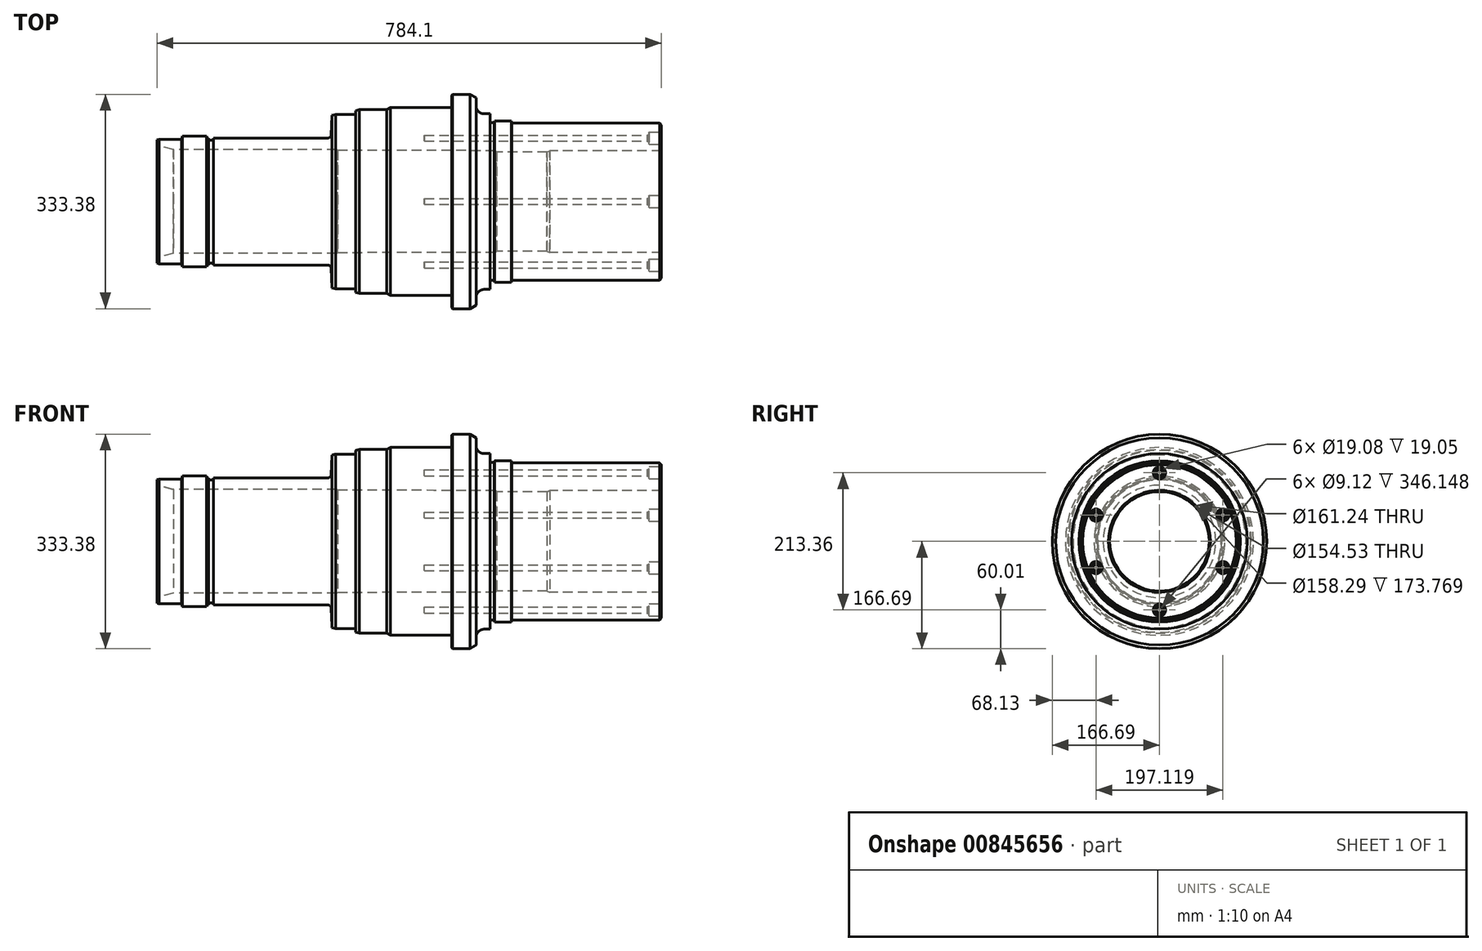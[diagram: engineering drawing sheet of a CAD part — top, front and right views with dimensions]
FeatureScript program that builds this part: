
annotation { "Feature Type Name" : "Feature", "Feature Type Description" : "" }
export const myFeature = defineFeature(function(context is Context, id is Id, definition is map)
    precondition{}
    {
        {
            var Q0;
            Q0=qCreatedBy(makeId("Front.planeOp"),FACE);
            var sketch = newSketch(context, id + "F0", { "sketchPlane" : qUnion([Q0])});
            skLineSegment(sketch, "E0", {"start": v(0, 0) * mm, "end": v(784.1, 0) * mm, "construction": true});
            skLineSegment(sketch, "E1", {"start": v(0, 96.84) * mm, "end": v(38.1, 96.84) * mm});
            skLineSegment(sketch, "E2", {"start": v(25.55, 80.62) * mm, "end": v(279.4, 80.62) * mm});
            skLineSegment(sketch, "E3", {"start": v(39.38, 101.6) * mm, "end": v(77, 101.6) * mm});
            skLineSegment(sketch, "E4", {"start": v(77.72, 98.87) * mm, "end": v(80.16, 98.87) * mm});
            skLineSegment(sketch, "E5", {"start": v(80.16, 98.87) * mm, "end": v(80.16, 95.7) * mm});
            skLineSegment(sketch, "E6", {"start": v(80.16, 95.7) * mm, "end": v(88.09, 95.7) * mm});
            skLineSegment(sketch, "E7", {"start": v(88.09, 95.7) * mm, "end": v(88.09, 98.87) * mm});
            skLineSegment(sketch, "E8", {"start": v(88.09, 98.87) * mm, "end": v(270.59, 98.87) * mm});
            skLineSegment(sketch, "E9", {"start": v(272.2, 135.64) * mm, "end": v(308.69, 135.64) * mm});
            skLineSegment(sketch, "E10", {"start": v(308.69, 135.64) * mm, "end": v(308.69, 142.88) * mm});
            skLineSegment(sketch, "E11", {"start": v(308.69, 142.88) * mm, "end": v(357.2, 142.88) * mm});
            skLineSegment(sketch, "E12", {"start": v(357.2, 142.87) * mm, "end": v(362.7, 146.05) * mm});
            skLineSegment(sketch, "E13", {"start": v(362.7, 146.05) * mm, "end": v(457.99, 146.05) * mm});
            skLineSegment(sketch, "E14", {"start": v(457.99, 146.05) * mm, "end": v(457.99, 166.69) * mm});
            skLineSegment(sketch, "E15", {"start": v(457.99, 166.69) * mm, "end": v(495.94, 166.69) * mm});
            skLineSegment(sketch, "E16", {"start": v(495.94, 166.69) * mm, "end": v(495.94, 136.53) * mm});
            skLineSegment(sketch, "E17", {"start": v(495.94, 136.53) * mm, "end": v(517.52, 136.53) * mm});
            skLineSegment(sketch, "E18", {"start": v(517.52, 136.53) * mm, "end": v(517.52, 122.5) * mm});
            skLineSegment(sketch, "E19", {"start": v(517.52, 122.5) * mm, "end": v(523.88, 122.5) * mm});
            skLineSegment(sketch, "E20", {"start": v(523.88, 122.5) * mm, "end": v(524.65, 125.41) * mm});
            skLineSegment(sketch, "E21", {"start": v(524.65, 125.41) * mm, "end": v(550.85, 125.41) * mm});
            skLineSegment(sketch, "E22", {"start": v(550.85, 125.41) * mm, "end": v(551.7, 122.24) * mm});
            skLineSegment(sketch, "E23", {"start": v(551.7, 122.24) * mm, "end": v(784.1, 122.24) * mm});
            skLineSegment(sketch, "E24", {"start": v(784.1, 79.15) * mm, "end": v(784.1, 122.24) * mm});
            skLineSegment(sketch, "E25", {"start": v(784.1, 79.15) * mm, "end": v(610.33, 79.15) * mm});
            skLineSegment(sketch, "E26", {"start": v(610.33, 79.15) * mm, "end": v(606.3, 77.27) * mm});
            skLineSegment(sketch, "E27", {"start": v(606.3, 77.27) * mm, "end": v(527.92, 77.27) * mm});
            skLineSegment(sketch, "E28", {"start": v(279.4, 80.62) * mm, "end": v(281.23, 79.57) * mm});
            skLineSegment(sketch, "E29", {"start": v(281.23, 79.57) * mm, "end": v(526.04, 79.15) * mm});
            skLineSegment(sketch, "E30", {"start": v(527.92, 77.27) * mm, "end": v(526.04, 79.15) * mm});
            skLineSegment(sketch, "E31", {"start": v(270.59, 98.87) * mm, "end": v(272.2, 135.64) * mm});
            skLineSegment(sketch, "E32", {"start": v(38.1, 96.84) * mm, "end": v(39.38, 101.6) * mm});
            skLineSegment(sketch, "E33", {"start": v(77.72, 98.87) * mm, "end": v(77, 101.6) * mm});
            skPoint(sketch, "E34.end.orphan", {"position": v(38.1, 101.6) * mm});
            skLineSegment(sketch, "E35", {"start": v(0, 87.46) * mm, "end": v(25.55, 80.62) * mm});
            skLineSegment(sketch, "E36", {"start": v(0, 96.84) * mm, "end": v(0, 87.46) * mm});
            skSolve(sketch);
        }
        {
            var Q0;
            Q0 = qSketchRegion(id + "F0", true);
            var Q1;
            Q1=sQuery(id+"F0.wireOp",EDGE,"E0");
            revolve(context, id + "F1", {"surfaceOperationType" : NewSurfaceOperationType.NEW, "entities" : qUnion([Q0]), "axis" : qUnion([Q1]), "revolveType" : RevolveType.FULL});
        }
        {
            var Q0;
            Q0=makeQuery(id+"F1.opRevolve","SWEPT_EDGE",EDGE,{"disambiguationData":[OSD([sQuery(id+"F0.wireOp",EDGE,"E15"),sQuery(id+"F0.wireOp",EDGE,"E16")])]});
            chamfer(context, id + "F2", {"entities" : qUnion([Q0]), "chamferType" : ChamferType.OFFSET_ANGLE, "width" : 9.52 * mm, "oppositeDirection" : false, "angle" : 30 * degree, "tangentPropagation" : true});
        }
        {
            var Q0;
            Q0=makeQuery(id+"F1.opRevolve","SWEPT_EDGE",EDGE,{"disambiguationData":[OSD([sQuery(id+"F0.wireOp",EDGE,"E16"),sQuery(id+"F0.wireOp",EDGE,"E17")])]});
            fillet(context, id + "F3", {"entities" : qUnion([Q0]), "radius" : 12.7 * mm, "tangentPropagation" : true, "allowEdgeOverflow" : false});
        }
        {
            var Q0;
            Q0=makeQuery(id+"F1.opRevolve","SWEPT_EDGE",EDGE,{"disambiguationData":[OSD([sQuery(id+"F0.wireOp",EDGE,"E8"),sQuery(id+"F0.wireOp",EDGE,"E31")])]});
            fillet(context, id + "F4", {"entities" : qUnion([Q0]), "radius" : 5.08 * mm, "tangentPropagation" : true, "allowEdgeOverflow" : false});
        }
        {
            var Q0;
            Q0=makeQuery(id+"F1.opRevolve","SWEPT_EDGE",EDGE,{"disambiguationData":[OSD([sQuery(id+"F0.wireOp",EDGE,"E9"),sQuery(id+"F0.wireOp",EDGE,"E31")])]});
            var Q1;
            Q1=makeQuery(id+"F1.opRevolve","SWEPT_EDGE",EDGE,{"disambiguationData":[OSD([sQuery(id+"F0.wireOp",EDGE,"E10"),sQuery(id+"F0.wireOp",EDGE,"E11")])]});
            chamfer(context, id + "F5", {"entities" : qUnion([Q0, Q1]), "chamferType" : ChamferType.OFFSET_ANGLE, "width" : 1.27 * mm, "oppositeDirection" : false, "angle" : 75 * degree, "tangentPropagation" : true});
        }
        {
            var Q0;
            Q0=makeQuery(id+"F1.opRevolve","SWEPT_EDGE",EDGE,{"disambiguationData":[OSD([sQuery(id+"F0.wireOp",EDGE,"E1"),sQuery(id+"F0.wireOp",EDGE,"SCYpA8kQ-7sTV-xUNJ-m1pp-K6qHX3d4gstn")])]});
            chamfer(context, id + "F6", {"entities" : qUnion([Q0]), "chamferType" : ChamferType.OFFSET_ANGLE, "width" : 0.86 * mm, "oppositeDirection" : false, "angle" : 75 * degree, "tangentPropagation" : true});
        }
        {
            var Q0;
            Q0=makeQuery(id+"F1.opRevolve","SWEPT_EDGE",EDGE,{"disambiguationData":[OSD([sQuery(id+"F0.wireOp",EDGE,"E23"),sQuery(id+"F0.wireOp",EDGE,"E24")])]});
            chamfer(context, id + "F7", {"entities" : qUnion([Q0]), "width" : 3.05 * mm, "tangentPropagation" : true});
        }
        {
            var Q0;
            Q0=makeQuery(id+"F1.opRevolve","SWEPT_EDGE",EDGE,{"disambiguationData":[OSD([sQuery(id+"F0.wireOp",EDGE,"E14"),sQuery(id+"F0.wireOp",EDGE,"E15")])]});
            chamfer(context, id + "F8", {"entities" : qUnion([Q0]), "width" : 1.52 * mm, "tangentPropagation" : true});
        }
        {
            var Q0;
            Q0=makeQuery(id+"F1.opRevolve","SWEPT_FACE",FACE,{"disambiguationData":[OSD([sQuery(id+"F0.wireOp",EDGE,"E24")])]});
            var sketch = newSketch(context, id + "F9", { "sketchPlane" : qUnion([Q0])});
            skCircle(sketch, "E37", {"center": v(0, 106.68) * mm, "radius": 4.56 * mm});
            skCircle(sketch, "E38", {"center": v(0, -106.68) * mm, "radius": 4.56 * mm});
            skCircle(sketch, "E39", {"center": v(98.52, 40.92) * mm, "radius": 4.56 * mm});
            skCircle(sketch, "E40", {"center": v(98.56, -40.82) * mm, "radius": 4.56 * mm});
            skCircle(sketch, "E41", {"center": v(-98.56, -40.82) * mm, "radius": 4.56 * mm});
            skCircle(sketch, "E42", {"center": v(-98.56, 40.83) * mm, "radius": 4.56 * mm});
            skLineSegment(sketch, "E43", {"start": v(-107.72, 0) * mm, "end": v(113.39, 0) * mm, "construction": true});
            skLineSegment(sketch, "E44", {"start": v(0, 0) * mm, "end": v(98.52, 40.92) * mm, "construction": true});
            skLineSegment(sketch, "E45", {"start": v(0, 0) * mm, "end": v(-98.56, 40.83) * mm, "construction": true});
            skLineSegment(sketch, "E46", {"start": v(0, 0) * mm, "end": v(-98.56, -40.82) * mm, "construction": true});
            skLineSegment(sketch, "E47", {"start": v(0, 0) * mm, "end": v(98.56, -40.82) * mm, "construction": true});
            skSolve(sketch);
        }
        {
            var Q0;
            Q0 = qSketchRegion(id + "F9", true);
            extrude(context, id + "F10", {"entities" : qUnion([Q0]), "operationType" : NewBodyOperationType.REMOVE, "oppositeDirection" : true, "depth" : 368.3 * mm, "offsetDistance" : 25.4 * mm});
        }
        {
            var Q0;
            Q0=makeQuery(id+"F1.opRevolve","SWEPT_FACE",FACE,{"disambiguationData":[OSD([sQuery(id+"F0.wireOp",EDGE,"E24")])]});
            var sketch = newSketch(context, id + "F11", { "sketchPlane" : qUnion([Q0])});
            skCircle(sketch, "E48", {"center": v(98.52, 40.92) * mm, "radius": 9.54 * mm});
            skCircle(sketch, "E49", {"center": v(0, 106.68) * mm, "radius": 9.54 * mm});
            skCircle(sketch, "E50", {"center": v(-98.56, 40.83) * mm, "radius": 9.54 * mm});
            skCircle(sketch, "E51", {"center": v(-98.56, -40.82) * mm, "radius": 9.54 * mm});
            skCircle(sketch, "E52", {"center": v(98.56, -40.82) * mm, "radius": 9.54 * mm});
            skCircle(sketch, "E53", {"center": v(0, -106.68) * mm, "radius": 9.54 * mm});
            skSolve(sketch);
        }
        {
            var Q0;
            Q0 = qSketchRegion(id + "F11", true);
            extrude(context, id + "F12", {"entities" : qUnion([Q0]), "operationType" : NewBodyOperationType.REMOVE, "oppositeDirection" : true, "depth" : 19.05 * mm, "offsetDistance" : 25.4 * mm});
        }
        {
            var Q0;
            Q0=makeQuery(id+"F12.boolean.opBoolean","INTERSECT",EDGE,{"derivedFrom":[makeQuery(id+"F10.boolean.opBoolean","COPY",FACE,{"derivedFrom":makeQuery(id+"F10.opExtrude","SWEPT_FACE",FACE,{"disambiguationData":[OSD([sQuery(id+"F9.wireOp",EDGE,"E37")])]})}),makeQuery(id+"F12.opExtrude","CAP_FACE",FACE,{"disambiguationData":[OSD([sQuery(id+"F11.wireOp",EDGE,"E49")])],"isStart":false})]});
            var Q1;
            Q1=makeQuery(id+"F12.boolean.opBoolean","INTERSECT",EDGE,{"derivedFrom":[makeQuery(id+"F10.boolean.opBoolean","COPY",FACE,{"derivedFrom":makeQuery(id+"F10.opExtrude","SWEPT_FACE",FACE,{"disambiguationData":[OSD([sQuery(id+"F9.wireOp",EDGE,"E42")])]})}),makeQuery(id+"F12.opExtrude","CAP_FACE",FACE,{"disambiguationData":[OSD([sQuery(id+"F11.wireOp",EDGE,"E50")])],"isStart":false})]});
            var Q2;
            Q2=makeQuery(id+"F12.boolean.opBoolean","INTERSECT",EDGE,{"derivedFrom":[makeQuery(id+"F10.boolean.opBoolean","COPY",FACE,{"derivedFrom":makeQuery(id+"F10.opExtrude","SWEPT_FACE",FACE,{"disambiguationData":[OSD([sQuery(id+"F9.wireOp",EDGE,"E38")])]})}),makeQuery(id+"F12.opExtrude","CAP_FACE",FACE,{"disambiguationData":[OSD([sQuery(id+"F11.wireOp",EDGE,"E53")])],"isStart":false})]});
            var Q3;
            Q3=makeQuery(id+"F12.boolean.opBoolean","INTERSECT",EDGE,{"derivedFrom":[makeQuery(id+"F10.boolean.opBoolean","COPY",FACE,{"derivedFrom":makeQuery(id+"F10.opExtrude","SWEPT_FACE",FACE,{"disambiguationData":[OSD([sQuery(id+"F9.wireOp",EDGE,"E41")])]})}),makeQuery(id+"F12.opExtrude","CAP_FACE",FACE,{"disambiguationData":[OSD([sQuery(id+"F11.wireOp",EDGE,"E51")])],"isStart":false})]});
            var Q4;
            Q4=makeQuery(id+"F12.boolean.opBoolean","INTERSECT",EDGE,{"derivedFrom":[makeQuery(id+"F10.boolean.opBoolean","COPY",FACE,{"derivedFrom":makeQuery(id+"F10.opExtrude","SWEPT_FACE",FACE,{"disambiguationData":[OSD([sQuery(id+"F9.wireOp",EDGE,"E40")])]})}),makeQuery(id+"F12.opExtrude","CAP_FACE",FACE,{"disambiguationData":[OSD([sQuery(id+"F11.wireOp",EDGE,"E52")])],"isStart":false})]});
            var Q5;
            Q5=makeQuery(id+"F12.boolean.opBoolean","INTERSECT",EDGE,{"derivedFrom":[makeQuery(id+"F10.boolean.opBoolean","COPY",FACE,{"derivedFrom":makeQuery(id+"F10.opExtrude","SWEPT_FACE",FACE,{"disambiguationData":[OSD([sQuery(id+"F9.wireOp",EDGE,"E39")])]})}),makeQuery(id+"F12.opExtrude","CAP_FACE",FACE,{"disambiguationData":[OSD([sQuery(id+"F11.wireOp",EDGE,"E48")])],"isStart":false})]});
            chamfer(context, id + "F13", {"entities" : qUnion([Q0, Q1, Q2, Q3, Q4, Q5]), "chamferType" : ChamferType.OFFSET_ANGLE, "width" : 1.8 * mm, "oppositeDirection" : false, "angle" : 60 * degree, "tangentPropagation" : true});
        }
    });
